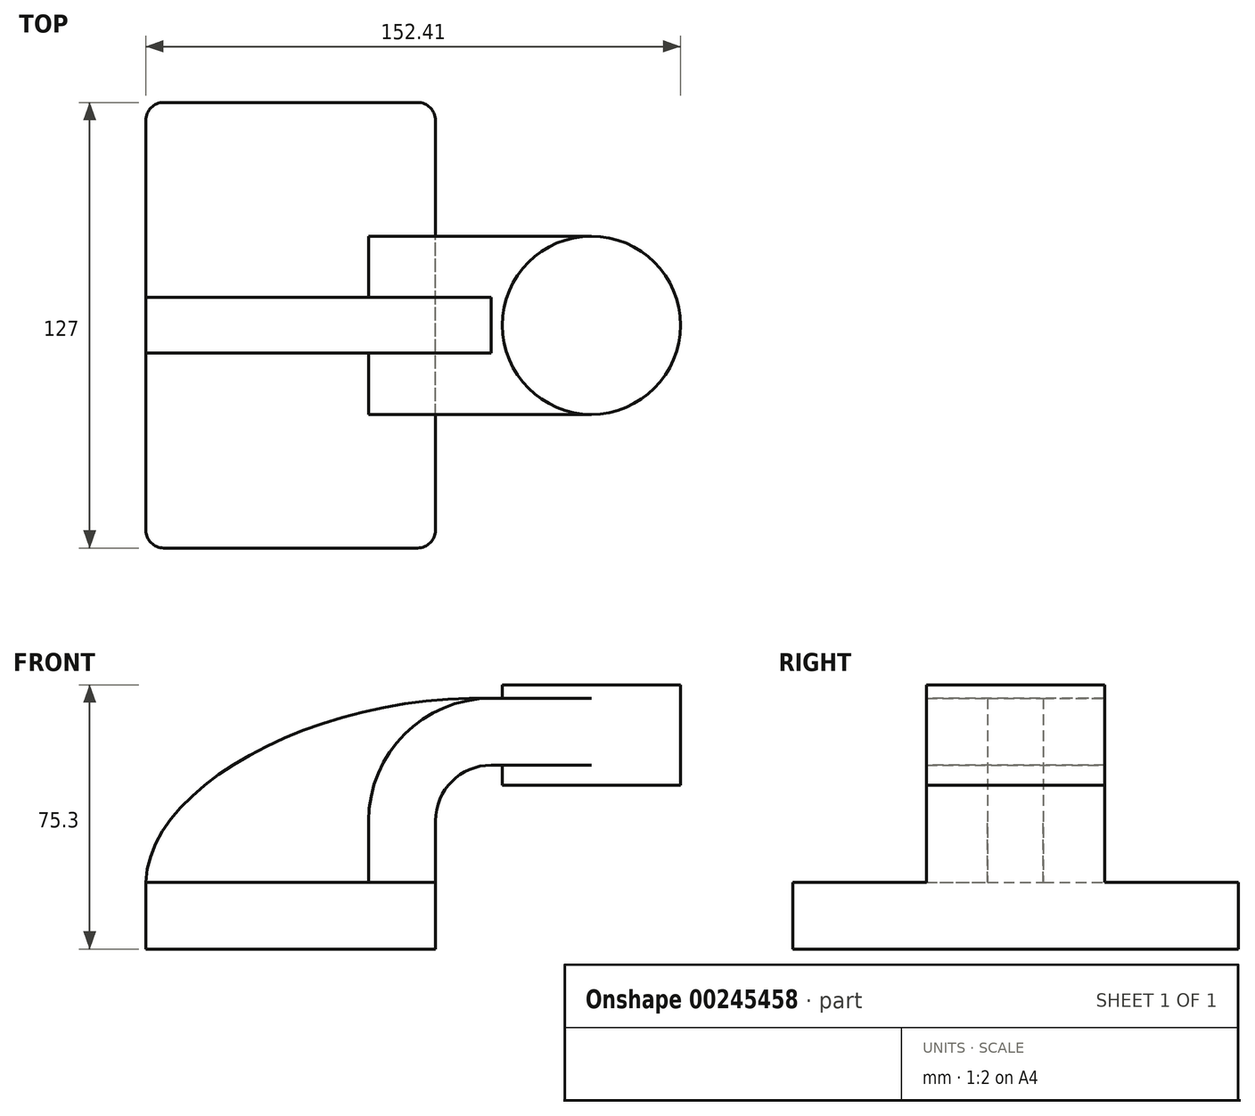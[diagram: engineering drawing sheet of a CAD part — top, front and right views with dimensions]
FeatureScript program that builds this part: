
annotation { "Feature Type Name" : "Feature", "Feature Type Description" : "" }
export const myFeature = defineFeature(function(context is Context, id is Id, definition is map)
    precondition{}
    {
        {
            var Q0;
            Q0=qCreatedBy(makeId("Front.planeOp"),FACE);
            var sketch = newSketch(context, id + "F0", { "sketchPlane" : qUnion([Q0])});
            skLineSegment(sketch, "E0.bottom", {"start": v(41.27, 9.53) * mm, "end": v(-41.28, 9.53) * mm});
            skLineSegment(sketch, "E0.top", {"start": v(41.28, -9.52) * mm, "end": v(-41.27, -9.52) * mm});
            skLineSegment(sketch, "E0.left", {"start": v(41.27, 9.53) * mm, "end": v(41.28, -9.52) * mm});
            skLineSegment(sketch, "E0.right", {"start": v(-41.28, 9.53) * mm, "end": v(-41.27, -9.52) * mm});
            skPoint(sketch, "E0.middle", {"position": v(0, 0) * mm});
            skLineSegment(sketch, "E1.bottom", {"start": v(111.13, 65.77) * mm, "end": v(60.32, 65.77) * mm});
            skLineSegment(sketch, "E1.top", {"start": v(111.13, 37.2) * mm, "end": v(60.32, 37.2) * mm});
            skLineSegment(sketch, "E1.left", {"start": v(111.13, 65.77) * mm, "end": v(111.13, 37.2) * mm});
            skLineSegment(sketch, "E1.right", {"start": v(60.32, 65.77) * mm, "end": v(60.32, 37.2) * mm});
            skPoint(sketch, "E1.middle", {"position": v(85.72, 51.49) * mm});
            skLineSegment(sketch, "E2", {"start": v(41.27, 9.53) * mm, "end": v(41.27, 27) * mm});
            skArc(sketch, "E3", {"start": v(41.27, 27) * mm, "mid": v(45.92, 38.23) * mm, "end": v(57.15, 42.88) * mm});
            skLineSegment(sketch, "E4", {"start": v(57.15, 42.88) * mm, "end": v(85.72, 42.88) * mm});
            skLineSegment(sketch, "E5.0", {"start": v(57.15, 61.93) * mm, "end": v(85.72, 61.93) * mm});
            skArc(sketch, "E5.1", {"start": v(22.22, 27) * mm, "mid": v(32.45, 51.7) * mm, "end": v(57.15, 61.93) * mm});
            skLineSegment(sketch, "E5.2", {"start": v(22.22, 9.53) * mm, "end": v(22.22, 27) * mm});
            skLineSegment(sketch, "E6", {"start": v(85.72, 61.93) * mm, "end": v(85.72, 51.49) * mm});
            skLineSegment(sketch, "E7", {"start": v(85.72, 51.49) * mm, "end": v(85.72, 42.88) * mm});
            skLineSegment(sketch, "E8", {"start": v(85.72, 61.93) * mm, "end": v(85.72, 65.77) * mm});
            skLineSegment(sketch, "E9", {"start": v(85.72, 42.88) * mm, "end": v(85.72, 37.2) * mm});
            skFitSpline(sketch, "E10", {"points": [v(57.15, 61.93) * mm, v(-41.28, 9.53) * mm], "startDerivative": vector(-141.74, 4.13) * mm, "endDerivative": vector(-3.31, -85.82) * mm});
            skSolve(sketch);
        }
        {
            var Q0;
            Q0=makeQuery(id+"F0.imprint","IMPRINT",FACE,{"disambiguationData":[TD([[makeQuery(id+"F0.imprint","IMPRINT",EDGE,{"derivedFrom":sQuery(id+"F0.wireOp",EDGE,"E0.top")}),-1.0]])]});
            extrude(context, id + "F1", {"entities" : qUnion([Q0]), "endBound" : BoundingType.SYMMETRIC, "depth" : 127 * mm});
        }
        {
            var Q0;
            {var subQ1=sQuery(id+"F0.wireOp",EDGE,"E2");Q0=makeQuery(id+"F0.imprint","IMPRINT",FACE,{"disambiguationData":[TD([[makeQuery(id+"F0.imprint","IMPRINT",EDGE,{"derivedFrom":subQ1}),1.0]])]});}
            var Q1;
            {var subQ0=sQuery(id+"F0.wireOp",EDGE,"E6");Q1=makeQuery(id+"F0.imprint","IMPRINT",FACE,{"disambiguationData":[TD([[makeQuery(id+"F0.imprint","IMPRINT",EDGE,{"derivedFrom":subQ0}),-1.0]])]});}
            extrude(context, id + "F2", {"entities" : qUnion([Q0, Q1]), "operationType" : NewBodyOperationType.ADD, "endBound" : BoundingType.SYMMETRIC, "depth" : 50.8 * mm});
        }
        {
            var Q0;
            {var subQ0=sQuery(id+"F0.wireOp",EDGE,"E1.left");Q0=makeQuery(id+"F0.imprint","IMPRINT",FACE,{"disambiguationData":[TD([[makeQuery(id+"F0.imprint","IMPRINT",EDGE,{"derivedFrom":subQ0}),-1.0]])]});}
            var Q1;
            Q1=sQuery(id+"F0.wireOp",EDGE,"E6");
            revolve(context, id + "F3", {"operationType" : NewBodyOperationType.ADD, "entities" : qUnion([Q0]), "axis" : qUnion([Q1]), "revolveType" : RevolveType.FULL});
        }
        {
            var Q0;
            {var subQ3=sQuery(id+"F0.wireOp",EDGE,"E5.2");Q0=makeQuery(id+"F0.imprint","IMPRINT",FACE,{"disambiguationData":[TD([[makeQuery(id+"F0.imprint","IMPRINT",EDGE,{"derivedFrom":subQ3}),1.0]])]});}
            extrude(context, id + "F4", {"entities" : qUnion([Q0]), "operationType" : NewBodyOperationType.ADD, "endBound" : BoundingType.SYMMETRIC, "depth" : 15.88 * mm});
        }
        {
            var Q0;
            Q0=makeQuery(id+"F1.opExtrude","CAP_EDGE",EDGE,{"disambiguationData":[OSD([sQuery(id+"F0.wireOp",EDGE,"E0.left")])],"isStart":true});
            var Q1;
            Q1=makeQuery(id+"F1.opExtrude","CAP_EDGE",EDGE,{"disambiguationData":[OSD([sQuery(id+"F0.wireOp",EDGE,"E0.right")])],"isStart":true});
            var Q2;
            Q2=makeQuery(id+"F1.opExtrude","CAP_EDGE",EDGE,{"disambiguationData":[OSD([sQuery(id+"F0.wireOp",EDGE,"E0.right")])],"isStart":false});
            var Q3;
            Q3=makeQuery(id+"F1.opExtrude","CAP_EDGE",EDGE,{"disambiguationData":[OSD([sQuery(id+"F0.wireOp",EDGE,"E0.left")])],"isStart":false});
            fillet(context, id + "F5", {"entities" : qUnion([Q0, Q1, Q2, Q3]), "radius" : 5.08 * mm, "tangentPropagation" : true, "allowEdgeOverflow" : false});
        }
    });
